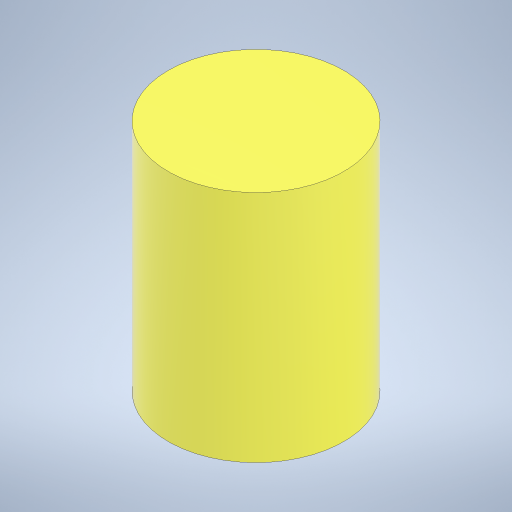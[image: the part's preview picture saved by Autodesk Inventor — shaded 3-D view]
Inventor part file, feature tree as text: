
AUTODESK INVENTOR PART (.ipt)
format: ipt  version: 2024.3 (Build 283343000, 343)  size: 203,264 bytes
history: native  units: mm
features: extrude x1, sketch x1
ambient origin geometry x8: Origin, YZ Plane, XZ Plane, XY Plane, X Axis, Y Axis, Z Axis, Center Point
bodies: Solid1 (feature_tree)
feature tree (2):
  extrude  "Extrusion1"  Depth=4.0mm TaperAngle=0.0deg
  sketch  "Sketch1"  dims[d0=3.0mm d1=4.0mm d2=0.0mm]
